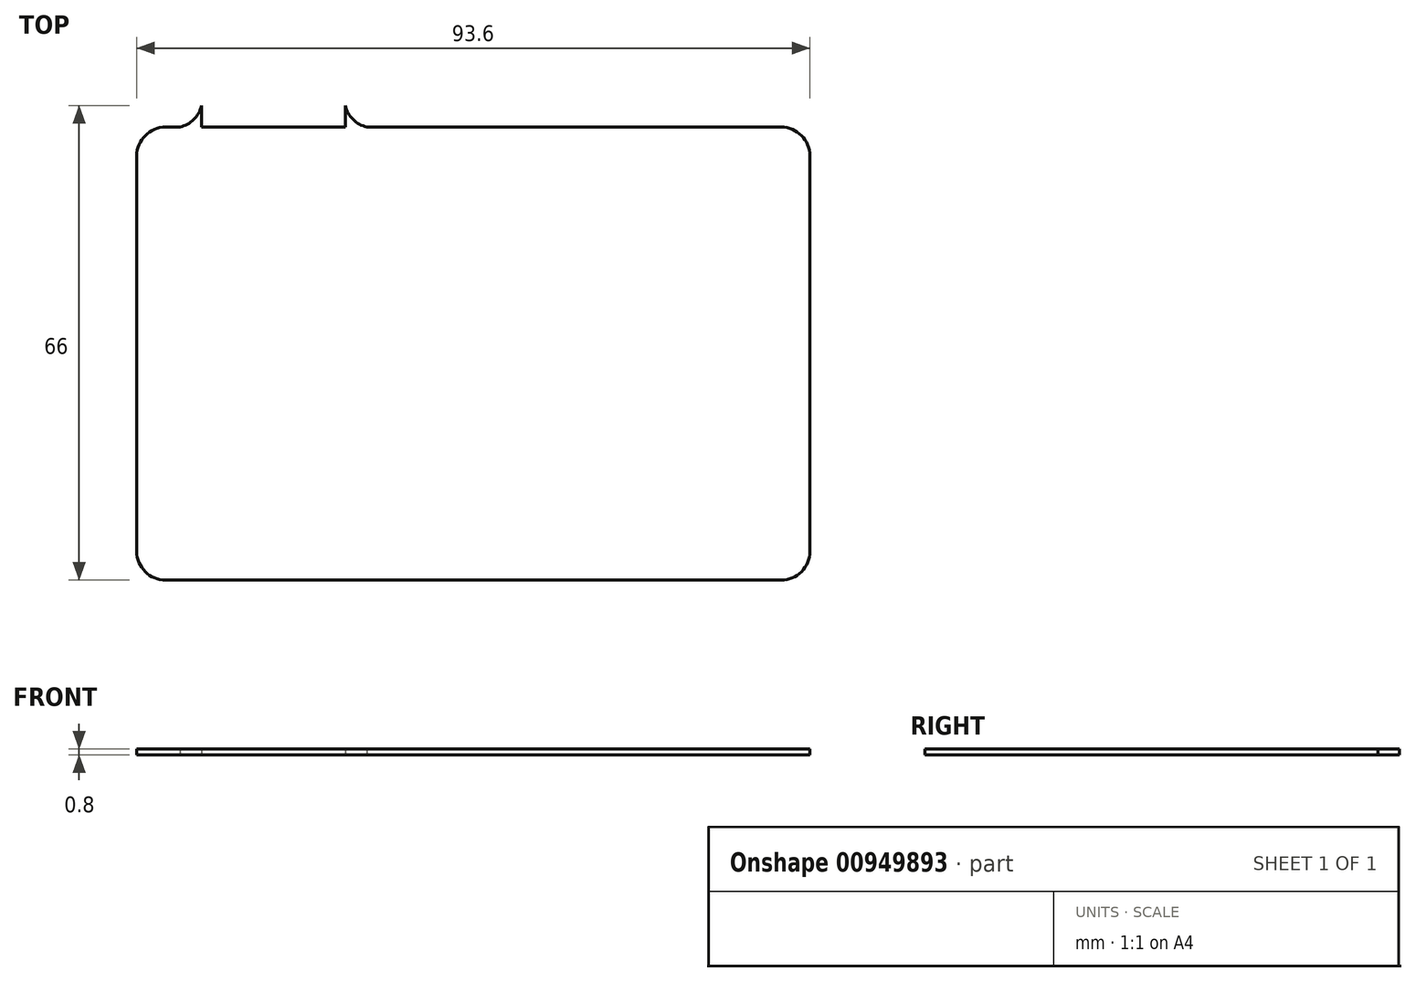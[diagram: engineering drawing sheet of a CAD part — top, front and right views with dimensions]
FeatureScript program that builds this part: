
annotation { "Feature Type Name" : "Feature", "Feature Type Description" : "" }
export const myFeature = defineFeature(function(context is Context, id is Id, definition is map)
    precondition{}
    {
        {
            var Q0;
            Q0=qCreatedBy(makeId("Top.planeOp"),FACE);
            var sketch = newSketch(context, id + "F0", { "sketchPlane" : qUnion([Q0])});
            skLineSegment(sketch, "E0.bottom", {"start": v(-34.53, 26.59) * mm, "end": v(51.07, 26.59) * mm});
            skLineSegment(sketch, "E0.top", {"start": v(-34.53, -36.41) * mm, "end": v(51.07, -36.41) * mm});
            skLineSegment(sketch, "E0.left", {"start": v(-38.53, 22.59) * mm, "end": v(-38.53, -32.41) * mm});
            skLineSegment(sketch, "E0.right", {"start": v(55.07, 22.59) * mm, "end": v(55.07, -32.41) * mm});
            skLineSegment(sketch, "E1.bottom", {"start": v(-29.53, 26.59) * mm, "end": v(-9.53, 26.59) * mm});
            skLineSegment(sketch, "E1.top", {"start": v(-25.53, 38.59) * mm, "end": v(-13.53, 38.59) * mm});
            skLineSegment(sketch, "E1.left", {"start": v(-29.53, 26.59) * mm, "end": v(-29.53, 34.59) * mm});
            skLineSegment(sketch, "E1.right", {"start": v(-9.53, 26.59) * mm, "end": v(-9.53, 34.59) * mm});
            skPoint(sketch, "E2.visualSharp", {"position": v(-38.53, -36.41) * mm});
            skArc(sketch, "E2.filletArc", {"start": v(-38.53, -32.41) * mm, "mid": v(-37.36, -35.24) * mm, "end": v(-34.53, -36.41) * mm});
            skPoint(sketch, "E3.visualSharp", {"position": v(-38.53, 26.59) * mm});
            skArc(sketch, "E3.filletArc", {"start": v(-34.53, 26.59) * mm, "mid": v(-37.36, 25.42) * mm, "end": v(-38.53, 22.59) * mm});
            skPoint(sketch, "E4.visualSharp", {"position": v(55.07, 26.59) * mm});
            skArc(sketch, "E4.filletArc", {"start": v(55.07, 22.59) * mm, "mid": v(53.9, 25.42) * mm, "end": v(51.07, 26.59) * mm});
            skPoint(sketch, "E5.visualSharp", {"position": v(55.07, -36.41) * mm});
            skArc(sketch, "E5.filletArc", {"start": v(51.07, -36.41) * mm, "mid": v(53.9, -35.24) * mm, "end": v(55.07, -32.41) * mm});
            skPoint(sketch, "E6.visualSharp", {"position": v(-9.53, 38.59) * mm});
            skArc(sketch, "E6.filletArc", {"start": v(-9.53, 34.59) * mm, "mid": v(-10.7, 37.42) * mm, "end": v(-13.53, 38.59) * mm});
            skPoint(sketch, "E7.visualSharp", {"position": v(-29.53, 38.59) * mm});
            skArc(sketch, "E7.filletArc", {"start": v(-25.53, 38.59) * mm, "mid": v(-28.36, 37.42) * mm, "end": v(-29.53, 34.59) * mm});
            skArc(sketch, "E8", {"start": v(-9.53, 29.59) * mm, "mid": v(-8.46, 27.66) * mm, "end": v(-6.53, 26.59) * mm});
            skArc(sketch, "E9", {"start": v(-32.53, 26.59) * mm, "mid": v(-30.6, 27.66) * mm, "end": v(-29.53, 29.59) * mm});
            skSolve(sketch);
        }
        {
            var Q0;
            Q0=makeQuery(id+"F0.imprint","IMPRINT",FACE,{"disambiguationData":[TD([[makeQuery(id+"F0.imprint","IMPRINT",EDGE,{"derivedFrom":sQuery(id+"F0.wireOp",EDGE,"E0.top")}),1.0]])]});
            var Q1;
            {var subQ3=sQuery(id+"F0.wireOp",EDGE,"E1.bottom");Q1=makeQuery(id+"F0.imprint","IMPRINT",FACE,{"disambiguationData":[TD([[makeQuery(id+"F0.imprint","IMPRINT",EDGE,{"derivedFrom":subQ3}),1.0]])]});}
            var Q2;
            {var subQ3=sQuery(id+"F0.wireOp",EDGE,"E9");Q2=makeQuery(id+"F0.imprint","IMPRINT",FACE,{"disambiguationData":[TD([[makeQuery(id+"F0.imprint","IMPRINT",EDGE,{"derivedFrom":subQ3}),-1.0]])]});}
            var Q3;
            {var subQ3=sQuery(id+"F0.wireOp",EDGE,"E8");Q3=makeQuery(id+"F0.imprint","IMPRINT",FACE,{"disambiguationData":[TD([[makeQuery(id+"F0.imprint","IMPRINT",EDGE,{"derivedFrom":subQ3}),-1.0]])]});}
            extrude(context, id + "F1", {"entities" : qUnion([Q0, Q1, Q2, Q3]), "depth" : 0.8 * mm, "offsetDistance" : 25 * mm});
        }
    });
